# Revit family: Metal_Lockers-Salsbury_Industries-53000_Series-1_Wide_Units
name_source: partatom
category: Specialty Equipment
revit_build: Autodesk Revit 2016 (Build: 20150714_1515(x64)
units: mm (PartAtom-declared; Revit-internal decimal feet)

## family parameters
Always vertical = Yes
Cut with Voids When Loaded = No
OmniClass Number = 23.40.00.00
OmniClass Title = Equipment and Furnishings
Part Type = Normal
Room Calculation Point = No
Round Connector Dimension = Use Diameter
Shared = No
Work Plane-Based = No

## types (6) — shared parameters
Assembly Code = C1030310
Compartment Divider Height = 22.814 "
Door Location D1 = Metal Locker Doors-15 inch with Hasps : Triple Tier Door - 6 foot
Hasp Handle Material = Plastic - Salsbury Finish - Black
Hasp Plate Rivet Material = Steel -Salsbury Finish - Polished Steel
Individual Door Height = 23.189 "
Manufacturer = Salsbury Industries
MasterFormat Number = 10 51 13
MasterFormat Title = Lockers
OmniClass 23 Number = 23.40.00.00
OmniClass 23 Title = Equipment and Furnishings
Type Comments = 15" Wide Standard Metal Locker - Triple Tier
URL = www.lockers.com
Unit Height = 72 "
Version = 2.0 (02/28/18)
Width = 15.04 "

## per-type parameters (varying)
| type | Base Height | Depth | Description | Model | Sloping Hood Height | Standard Leg Base | Zee Base |
| 53165 - with Standard 6" High Legs | 6 " | 15.01 " | 1 Wide - 6 Feet High - 15 Inches Deep | 53165 | 8.682 " | Metal Locker Legs : 6" High - 15"W x 15"D | Metal Locker Zee Base : None |
| 53168 - with Standard 6" High Legs | 6 " | 18.01 " | 1 Wide - 6 Feet High - 18 Inches Deep | 53168 | 10.739 " | Metal Locker Legs : 6" High - 15"W x 18"D | Metal Locker Zee Base : None |
| 53165 - with 77575 Zee Base and 77550 Lockers without Legs | 4 " | 15.01 " | 1 Wide - 6 Feet High - 15 Inches Deep with Zee Base and Lockers without Legs | 53165 with 77575 and 77550 | 8.682 " | Metal Locker Legs : No Legs | Metal Locker Zee Base : 77575 - 15"W x 15"D |
| 53168 - with 77578 Zee Base and 77550 Lockers without Legs | 4 " | 18.01 " | 1 Wide - 6 Feet High - 18 Inches Deep with Zee Base and Lockers without Legs | 53168 with 77578 and 77550 | 10.739 " | Metal Locker Legs : No Legs | Metal Locker Zee Base : 77578 - 15"W x 18"D |
| 53165 - with 77550 Lockers without Legs | 0 " | 15.01 " | 1 Wide - 6 Feet High - 15 Inches Deep with Lockers without Legs | 53165 with 77550 | 8.682 " | Metal Locker Legs : No Legs | Metal Locker Zee Base : None |
| 53168 - with 77550 Lockers without Legs | 0 " | 18.01 " | 1 Wide - 6 Feet High - 18 Inches Deep with Lockers without Legs | 53168 with 77550 | 10.739 " | Metal Locker Legs : No Legs | Metal Locker Zee Base : None |

## geometry (parser evidence)
native form markers: Sweep x58
no freeform markers — native parametric forms only
